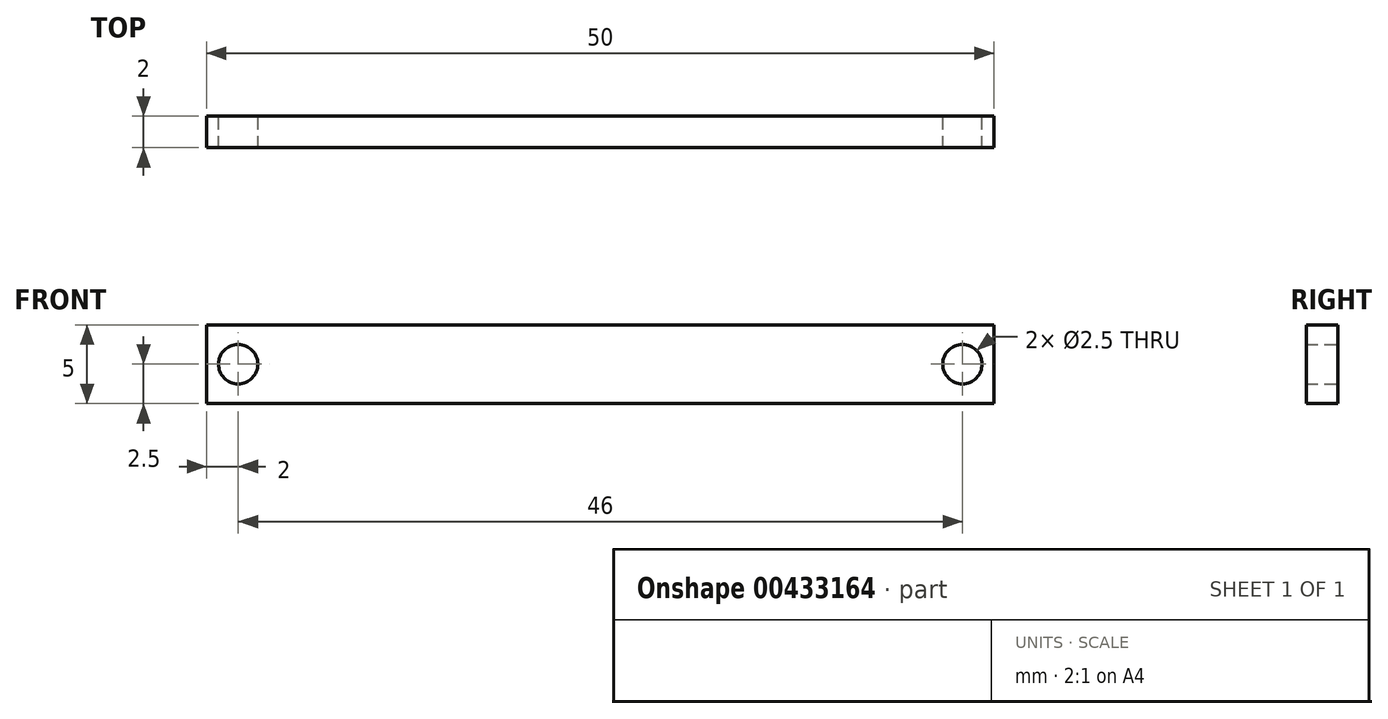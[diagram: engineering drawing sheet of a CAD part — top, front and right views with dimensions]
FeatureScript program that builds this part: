
annotation { "Feature Type Name" : "Feature", "Feature Type Description" : "" }
export const myFeature = defineFeature(function(context is Context, id is Id, definition is map)
    precondition{}
    {
        {
            var Q0;
            Q0=qCreatedBy(makeId("Front.planeOp"),FACE);
            var sketch = newSketch(context, id + "F0", { "sketchPlane" : qUnion([Q0])});
            skLineSegment(sketch, "E0.bottom", {"start": v(-25, 2.5) * mm, "end": v(25, 2.5) * mm});
            skLineSegment(sketch, "E0.top", {"start": v(-25, -2.5) * mm, "end": v(25, -2.5) * mm});
            skLineSegment(sketch, "E0.left", {"start": v(-25, 2.5) * mm, "end": v(-25, -2.5) * mm});
            skLineSegment(sketch, "E0.right", {"start": v(25, 2.5) * mm, "end": v(25, -2.5) * mm});
            skCircle(sketch, "E1", {"center": v(-23, 0) * mm, "radius": 1.25 * mm});
            skCircle(sketch, "E2.MirrorC", {"center": v(23, 0) * mm, "radius": 1.25 * mm});
            skSolve(sketch);
        }
        {
            var Q0;
            Q0=qSketchRegion(id+"F0",true);
            extrude(context, id + "F1", {"entities" : qUnion([Q0]), "depth" : 2 * mm});
        }
    });
